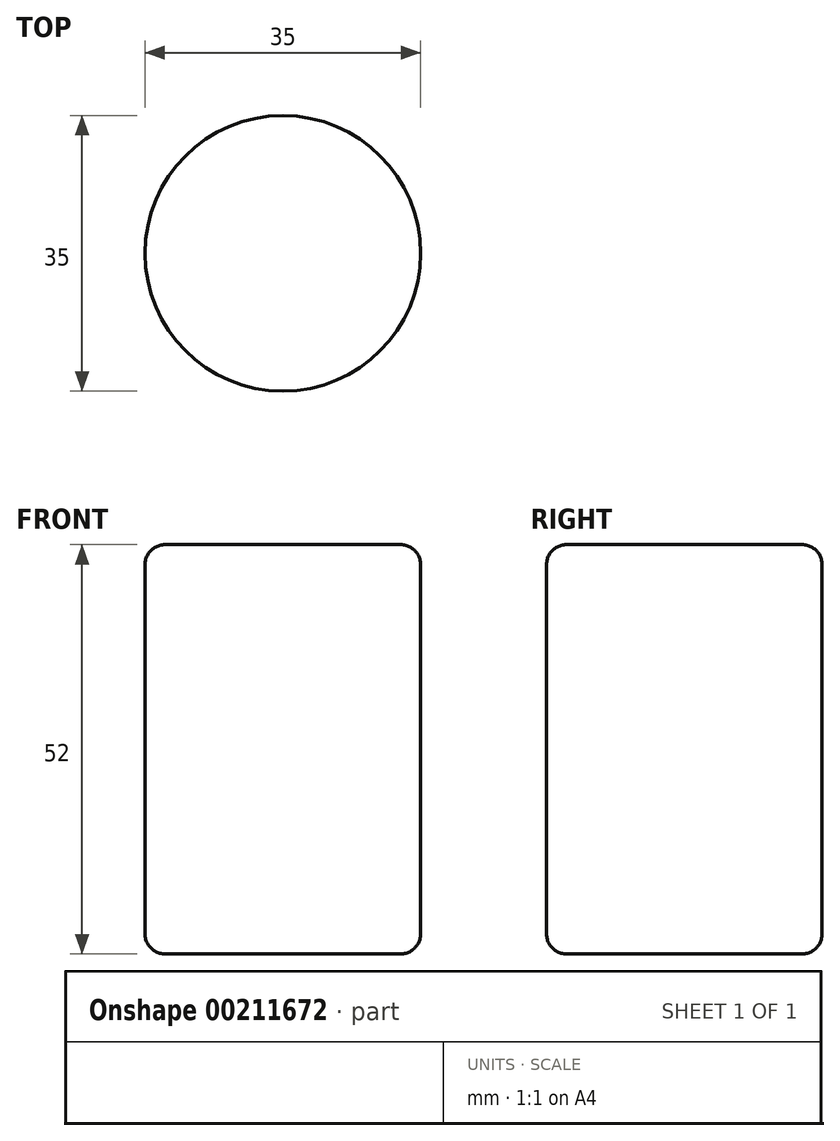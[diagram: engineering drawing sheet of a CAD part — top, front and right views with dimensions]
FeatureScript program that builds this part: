
annotation { "Feature Type Name" : "Feature", "Feature Type Description" : "" }
export const myFeature = defineFeature(function(context is Context, id is Id, definition is map)
    precondition{}
    {
        {
            var Q0;
            Q0=qCreatedBy(makeId("Front.planeOp"),FACE);
            var sketch = newSketch(context, id + "F0", { "sketchPlane" : qUnion([Q0])});
            skLineSegment(sketch, "E0.bottom", {"start": v(0, 0) * mm, "end": v(17.5, 0) * mm});
            skLineSegment(sketch, "E0.top", {"start": v(0, 52) * mm, "end": v(17.5, 52) * mm});
            skLineSegment(sketch, "E0.left", {"start": v(0, 0) * mm, "end": v(0, 52) * mm});
            skLineSegment(sketch, "E0.right", {"start": v(17.5, 0) * mm, "end": v(17.5, 52) * mm});
            skSolve(sketch);
        }
        {
            var Q0;
            Q0 = qSketchRegion(id + "F0", true);
            var Q1;
            Q1=sQuery(id+"F0.wireOp",EDGE,"E0.left");
            revolve(context, id + "F1", {"entities" : qUnion([Q0]), "axis" : qUnion([Q1]), "revolveType" : RevolveType.FULL});
        }
        {
            var Q0;
            Q0=makeQuery(id+"F1.opRevolve","SWEPT_EDGE",EDGE,{"disambiguationData":[OSD([sQuery(id+"F0.wireOp",EDGE,"E0.top"),sQuery(id+"F0.wireOp",EDGE,"E0.right")])]});
            var Q1;
            Q1=makeQuery(id+"F1.opRevolve","SWEPT_EDGE",EDGE,{"disambiguationData":[OSD([sQuery(id+"F0.wireOp",EDGE,"E0.bottom"),sQuery(id+"F0.wireOp",EDGE,"E0.right")])]});
            fillet(context, id + "F2", {"entities" : qUnion([Q0, Q1]), "radius" : 2.54 * mm, "tangentPropagation" : true, "allowEdgeOverflow" : false});
        }
    });
